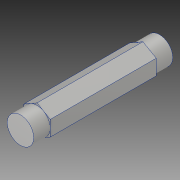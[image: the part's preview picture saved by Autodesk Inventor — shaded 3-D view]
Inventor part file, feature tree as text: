
AUTODESK INVENTOR PART (.ipt)
format: ipt  version: 2019 (Build 230136000, 136)  size: 117,760 bytes
history: native  units: in
note: dims shown in document units (in); Inventor stores cm internally (conversion verified against a paired STEP export)
features: extrude x2, sketch x2, mirror x1, projected_geometry x1
ambient origin geometry x8: Origin, YZ Plane, XZ Plane, XY Plane, X Axis, Y Axis, Z Axis, Center Point
bodies: Solid1 (feature_tree)
feature tree (6):
  extrude  "Extrusion1"  TaperAngle=0.0deg  [1 undecoded]
  extrude  "Extrusion2"  [1 undecoded]
  mirror  "Mirror1"
  sketch  "Sketch1"  dims[d2=0.0in d4=0.0in]
  sketch  "Sketch2"
  projected_geometry  "Projected Loop1"
note: 2 required parameter values undecoded (feature->parameter linkage not recoverable at this tier; creation-order binding heuristic only, values carry confidence <= 0.55)
